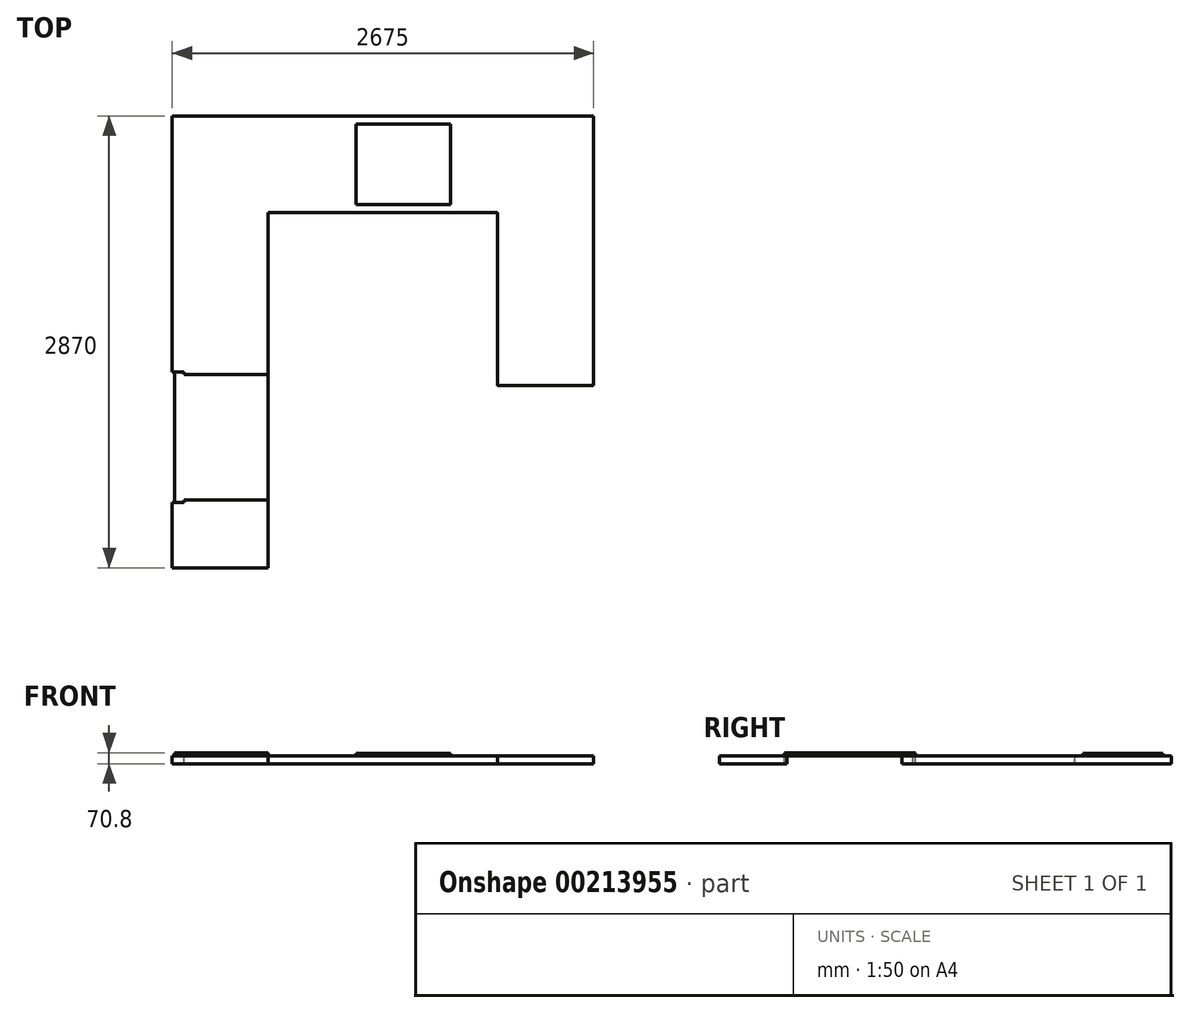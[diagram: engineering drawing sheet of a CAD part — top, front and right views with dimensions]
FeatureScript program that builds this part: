
annotation { "Feature Type Name" : "Feature", "Feature Type Description" : "" }
export const myFeature = defineFeature(function(context is Context, id is Id, definition is map)
    precondition{}
    {
        {
            var Q0;
            Q0=qCreatedBy(makeId("Top.planeOp"),FACE);
            var sketch = newSketch(context, id + "F0", { "sketchPlane" : qUnion([Q0])});
            skLineSegment(sketch, "E0", {"start": v(0, 0) * mm, "end": v(610, 0) * mm});
            skLineSegment(sketch, "E1", {"start": v(610, 0) * mm, "end": v(610, 430) * mm});
            skLineSegment(sketch, "E2", {"start": v(610, 2258) * mm, "end": v(2067, 2258) * mm});
            skLineSegment(sketch, "E3", {"start": v(2067, 2258) * mm, "end": v(2067, 1158) * mm});
            skLineSegment(sketch, "E4", {"start": v(2067, 1158) * mm, "end": v(2675, 1158) * mm});
            skLineSegment(sketch, "E5", {"start": v(2675, 1158) * mm, "end": v(2675, 2870) * mm});
            skLineSegment(sketch, "E6", {"start": v(2675, 2870) * mm, "end": v(0, 2870) * mm});
            skLineSegment(sketch, "E7", {"start": v(0, 2870) * mm, "end": v(0, 1244) * mm});
            skLineSegment(sketch, "E8", {"start": v(610, 1228) * mm, "end": v(73.67, 1228) * mm});
            skLineSegment(sketch, "E9", {"start": v(0, 1244) * mm, "end": v(73.67, 1244) * mm});
            skLineSegment(sketch, "E10", {"start": v(73.67, 414) * mm, "end": v(0, 414) * mm});
            skLineSegment(sketch, "E11", {"start": v(73.67, 1244) * mm, "end": v(73.67, 1228) * mm});
            skLineSegment(sketch, "E12.trimOffspring", {"start": v(610, 1228) * mm, "end": v(610, 2258) * mm});
            skLineSegment(sketch, "E13.trimOffspring", {"start": v(73.67, 430) * mm, "end": v(73.67, 414) * mm});
            skLineSegment(sketch, "E14.trimOffspring", {"start": v(0, 414) * mm, "end": v(0, 0) * mm});
            skLineSegment(sketch, "E15.trimOffspring", {"start": v(73.67, 430) * mm, "end": v(610, 430) * mm});
            skSolve(sketch);
        }
        {
            var Q0;
            Q0=makeQuery(id+"F0.imprint","IMPRINT",FACE,{"disambiguationData":[TD([[makeQuery(id+"F0.imprint","IMPRINT",EDGE,{"derivedFrom":sQuery(id+"F0.wireOp",EDGE,"E2")}),1.0]])]});
            var Q1;
            Q1=makeQuery(id+"F0.imprint","IMPRINT",FACE,{"disambiguationData":[TD([[makeQuery(id+"F0.imprint","IMPRINT",EDGE,{"derivedFrom":sQuery(id+"F0.wireOp",EDGE,"E0")}),1.0]])]});
            extrude(context, id + "F1", {"entities" : qUnion([Q0, Q1]), "oppositeDirection" : true, "depth" : 50.8 * mm});
        }
        {
            var Q0;
            Q0=makeQuery(id+"F1.opExtrude","CAP_FACE",FACE,{"disambiguationData":[OSD([sQuery(id+"F0.wireOp",EDGE,"E2"),sQuery(id+"F0.wireOp",EDGE,"E3"),sQuery(id+"F0.wireOp",EDGE,"E4"),sQuery(id+"F0.wireOp",EDGE,"E5"),sQuery(id+"F0.wireOp",EDGE,"E6"),sQuery(id+"F0.wireOp",EDGE,"E7"),sQuery(id+"F0.wireOp",EDGE,"E8"),sQuery(id+"F0.wireOp",EDGE,"E9"),sQuery(id+"F0.wireOp",EDGE,"E11"),sQuery(id+"F0.wireOp",EDGE,"E12.trimOffspring")])],"isStart":true});
            var sketch = newSketch(context, id + "F2", { "sketchPlane" : qUnion([Q0])});
            skLineSegment(sketch, "E16.bottom", {"start": v(1166, 2818) * mm, "end": v(1766, 2818) * mm});
            skLineSegment(sketch, "E16.top", {"start": v(1166, 2308) * mm, "end": v(1766, 2308) * mm});
            skLineSegment(sketch, "E16.left", {"start": v(1166, 2818) * mm, "end": v(1166, 2308) * mm});
            skLineSegment(sketch, "E16.right", {"start": v(1766, 2818) * mm, "end": v(1766, 2308) * mm});
            skLineSegment(sketch, "E17.0", {"start": v(610, 1228) * mm, "end": v(73.67, 1228) * mm, "construction": true});
            skLineSegment(sketch, "E17.1", {"start": v(73.67, 1244) * mm, "end": v(73.67, 1228) * mm, "construction": true});
            skLineSegment(sketch, "E17.2", {"start": v(15, 1244) * mm, "end": v(73.67, 1244) * mm, "construction": true});
            skLineSegment(sketch, "E17.3", {"start": v(73.67, 414) * mm, "end": v(15, 414) * mm, "construction": true});
            skLineSegment(sketch, "E17.4", {"start": v(73.67, 430) * mm, "end": v(73.67, 414) * mm, "construction": true});
            skLineSegment(sketch, "E17.5", {"start": v(73.67, 430) * mm, "end": v(610, 430) * mm, "construction": true});
            skLineSegment(sketch, "E18", {"start": v(610, 1228) * mm, "end": v(610, 430) * mm, "construction": true});
            skLineSegment(sketch, "E19", {"start": v(15, 1244) * mm, "end": v(15, 414) * mm, "construction": true});
            skPoint(sketch, "E20.orphan", {"position": v(0, 414) * mm});
            skPoint(sketch, "E21.orphan", {"position": v(0, 1244) * mm});
            skSolve(sketch);
        }
        {
            var Q0;
            Q0 = qSketchRegion(id + "F2", true);
            extrude(context, id + "F3", {"entities" : qUnion([Q0]), "depth" : 15 * mm});
        }
        {
            var Q0;
            Q0=makeQuery(id+"F1.opExtrude","CAP_FACE",FACE,{"disambiguationData":[OSD([sQuery(id+"F0.wireOp",EDGE,"E2"),sQuery(id+"F0.wireOp",EDGE,"E3"),sQuery(id+"F0.wireOp",EDGE,"E4"),sQuery(id+"F0.wireOp",EDGE,"E5"),sQuery(id+"F0.wireOp",EDGE,"E6"),sQuery(id+"F0.wireOp",EDGE,"E7"),sQuery(id+"F0.wireOp",EDGE,"E8"),sQuery(id+"F0.wireOp",EDGE,"E9"),sQuery(id+"F0.wireOp",EDGE,"E11"),sQuery(id+"F0.wireOp",EDGE,"E12.trimOffspring")])],"isStart":true});
            var sketch = newSketch(context, id + "F4", { "sketchPlane" : qUnion([Q0])});
            skLineSegment(sketch, "E22.0", {"start": v(610, 1228) * mm, "end": v(73.67, 1228) * mm});
            skLineSegment(sketch, "E22.1", {"start": v(15, 1244) * mm, "end": v(15, 414) * mm});
            skLineSegment(sketch, "E22.2", {"start": v(610, 1228) * mm, "end": v(610, 430) * mm});
            skLineSegment(sketch, "E22.3", {"start": v(73.67, 430) * mm, "end": v(610, 430) * mm});
            skLineSegment(sketch, "E22.4", {"start": v(73.67, 430) * mm, "end": v(73.67, 414) * mm});
            skLineSegment(sketch, "E22.5", {"start": v(73.67, 414) * mm, "end": v(15, 414) * mm});
            skPoint(sketch, "E22.6", {"position": v(73.67, 1236) * mm});
            skLineSegment(sketch, "E23", {"start": v(73.67, 1244) * mm, "end": v(15, 1244) * mm});
            skPoint(sketch, "E24.0.end.orphan", {"position": v(73.67, 1228) * mm});
            skLineSegment(sketch, "E25", {"start": v(73.67, 1244) * mm, "end": v(73.67, 1228) * mm});
            skSolve(sketch);
        }
        {
            var Q0;
            Q0 = qSketchRegion(id + "F4", true);
            extrude(context, id + "F5", {"entities" : qUnion([Q0]), "depth" : 20 * mm});
        }
        {
            var Q0;
            Q0=makeQuery(id+"F5.opExtrude","CAP_EDGE",EDGE,{"disambiguationData":[OSD([sQuery(id+"F4.wireOp",EDGE,"E22.2")])],"isStart":false});
            fillet(context, id + "F6", {"entities" : qUnion([Q0]), "radius" : 8 * mm, "tangentPropagation" : true, "allowEdgeOverflow" : false});
        }
        {
            var Q0;
            Q0=makeQuery(id+"F2.imprint","IMPRINT",FACE,{"disambiguationData":[TD([[makeQuery(id+"F2.imprint","IMPRINT",EDGE,{"derivedFrom":sQuery(id+"F2.wireOp",EDGE,"E16.bottom")}),1.0]])]});
            var sketch = newSketch(context, id + "F7", { "sketchPlane" : qUnion([Q0])});
            skLineSegment(sketch, "E26", {"start": v(2062.75, 1166.5) * mm, "end": v(2076.88, 1152.36) * mm});
            skLineSegment(sketch, "E27", {"start": v(2076.88, 1152.36) * mm, "end": v(2060.03, 1152.36) * mm});
            skLineSegment(sketch, "E28", {"start": v(2060.03, 1152.36) * mm, "end": v(2062.75, 1166.5) * mm});
            skSolve(sketch);
        }
        {
            var Q0;
            Q0 = qSketchRegion(id + "F7", true);
            extrude(context, id + "F8", {"entities" : qUnion([Q0]), "operationType" : NewBodyOperationType.REMOVE, "oppositeDirection" : true, "depth" : 7 * mm});
        }
    });
